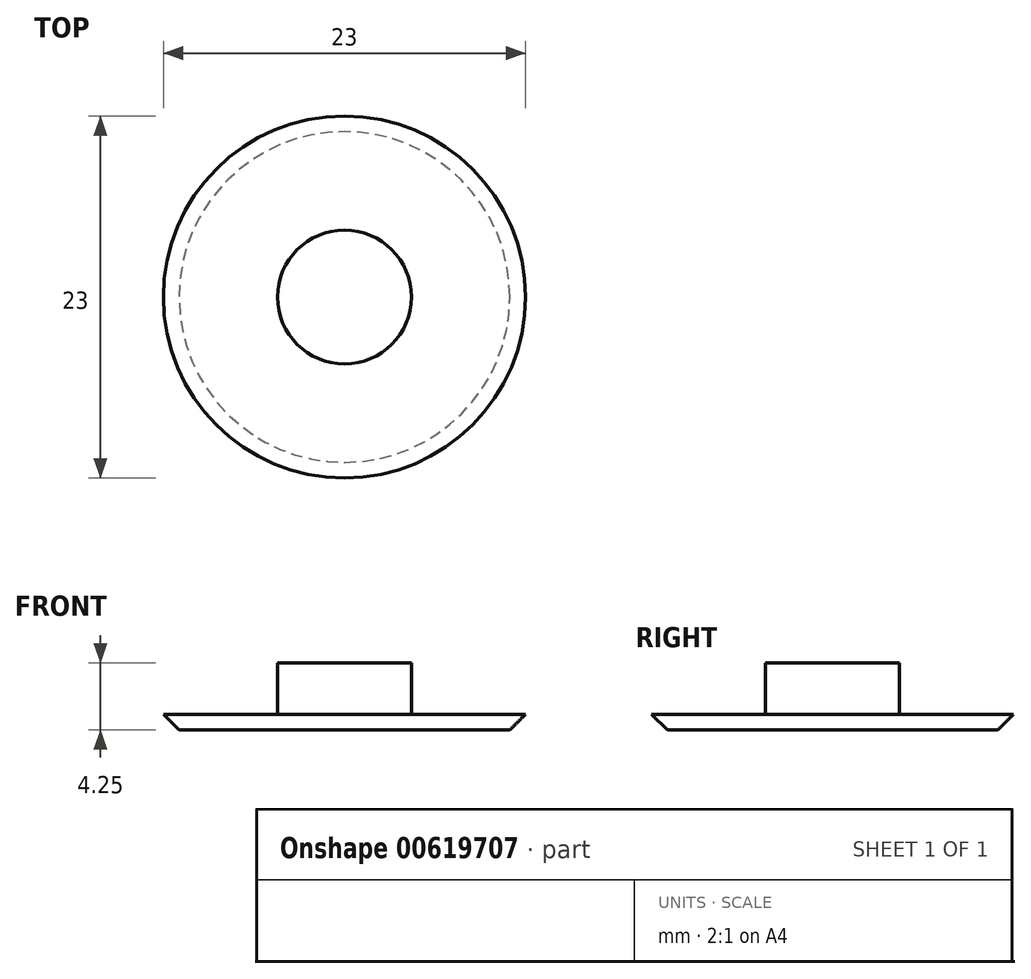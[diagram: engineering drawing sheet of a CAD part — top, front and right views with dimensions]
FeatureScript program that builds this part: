
annotation { "Feature Type Name" : "Feature", "Feature Type Description" : "" }
export const myFeature = defineFeature(function(context is Context, id is Id, definition is map)
    precondition{}
    {
        {
            var Q0;
            Q0=qCreatedBy(makeId("Top.planeOp"),FACE);
            var sketch = newSketch(context, id + "F0", { "sketchPlane" : qUnion([Q0])});
            skCircle(sketch, "E0", {"center": v(0, 0) * mm, "radius": 11.5 * mm});
            skSolve(sketch);
        }
        {
            var Q0;
            Q0=makeQuery(id+"F0.imprint","IMPRINT",FACE,{"disambiguationData":[TD([[makeQuery(id+"F0.imprint","IMPRINT",EDGE,{"derivedFrom":sQuery(id+"F0.wireOp",EDGE,"E0")}),1.0]])]});
            extrude(context, id + "F1", {"entities" : qUnion([Q0]), "depth" : 1 * mm, "offsetDistance" : 25 * mm});
        }
        {
            var Q0;
            Q0=makeQuery(id+"F1.opExtrude","CAP_FACE",FACE,{"disambiguationData":[OSD([sQuery(id+"F0.wireOp",EDGE,"E0")])],"isStart":false});
            var sketch = newSketch(context, id + "F2", { "sketchPlane" : qUnion([Q0])});
            skCircle(sketch, "E1", {"center": v(0, 0) * mm, "radius": 4.25 * mm});
            skSolve(sketch);
        }
        {
            var Q0;
            Q0=makeQuery(id+"F2.imprint","IMPRINT",FACE,{"disambiguationData":[TD([[makeQuery(id+"F2.imprint","IMPRINT",EDGE,{"derivedFrom":sQuery(id+"F2.wireOp",EDGE,"E1")}),1.0]])]});
            extrude(context, id + "F3", {"entities" : qUnion([Q0]), "operationType" : NewBodyOperationType.ADD, "depth" : 3.25 * mm, "offsetDistance" : 25 * mm});
        }
        {
            var Q0;
            Q0=makeQuery(id+"F1.opExtrude","CAP_EDGE",EDGE,{"disambiguationData":[OSD([sQuery(id+"F0.wireOp",EDGE,"E0")])],"isStart":true});
            chamfer(context, id + "F4", {"entities" : qUnion([Q0]), "width" : 1 * mm, "tangentPropagation" : true});
        }
    });
